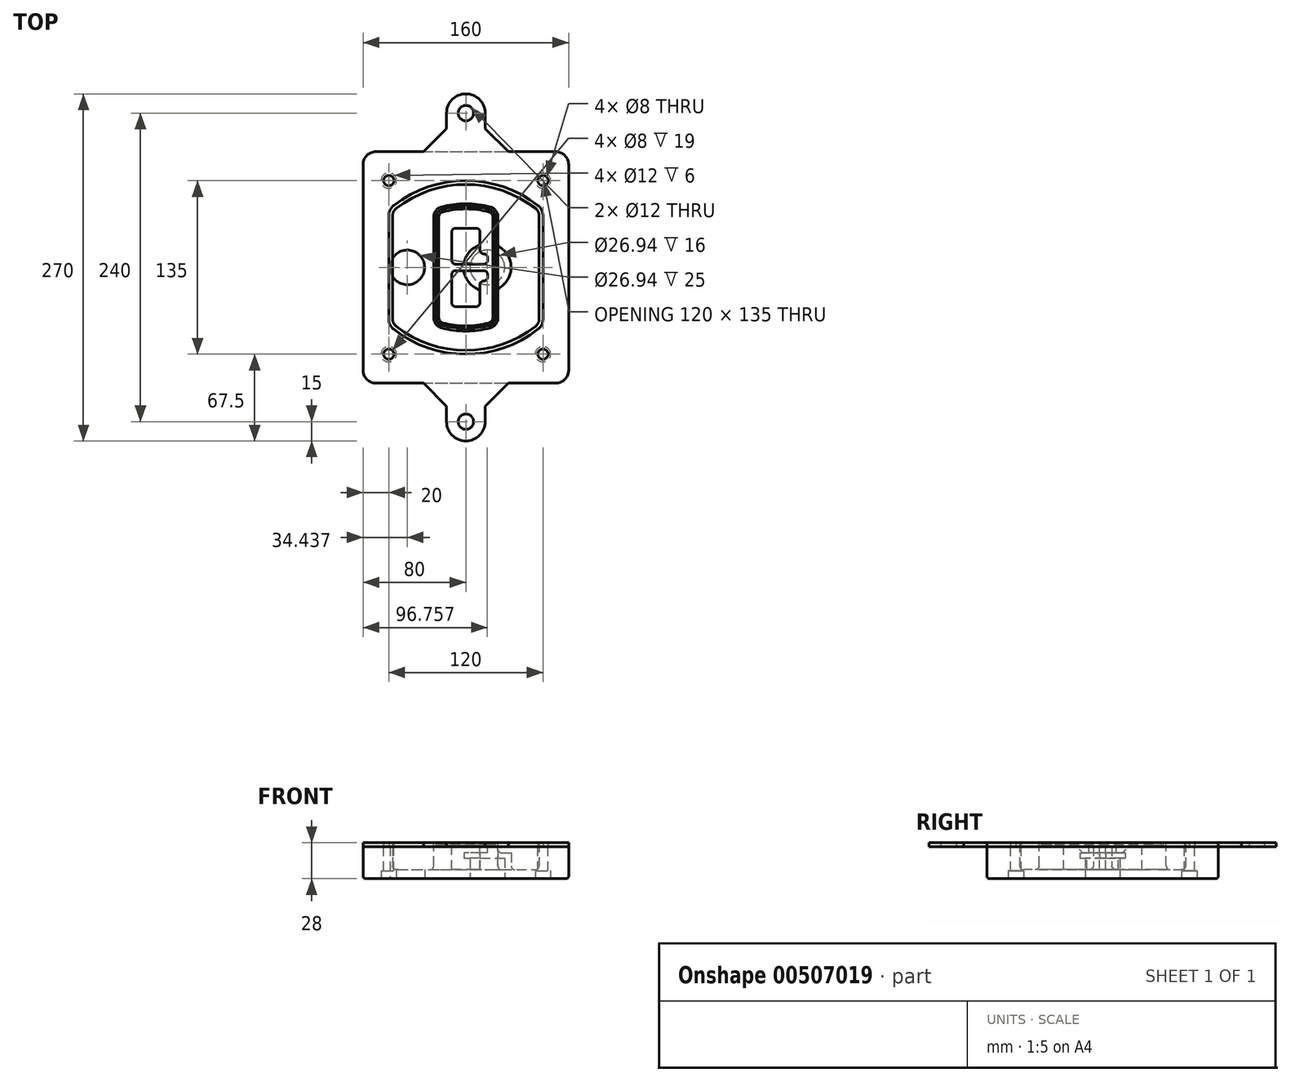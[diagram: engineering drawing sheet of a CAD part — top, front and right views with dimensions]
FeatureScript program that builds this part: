
annotation { "Feature Type Name" : "Feature", "Feature Type Description" : "" }
export const myFeature = defineFeature(function(context is Context, id is Id, definition is map)
    precondition{}
    {
        {
            var Q0;
            Q0=qCreatedBy(makeId("Top.planeOp"),FACE);
            var sketch = newSketch(context, id + "F0", { "sketchPlane" : qUnion([Q0])});
            skPoint(sketch, "E0.rect.middle", {"position": v(0, 0) * mm});
            skLineSegment(sketch, "E1.bottom", {"start": v(-70, -90) * mm, "end": v(70, -90) * mm});
            skLineSegment(sketch, "E1.top", {"start": v(-70, 90) * mm, "end": v(70, 90) * mm});
            skLineSegment(sketch, "E1.left", {"start": v(-80, -80) * mm, "end": v(-80, 80) * mm});
            skLineSegment(sketch, "E1.right", {"start": v(80, -80) * mm, "end": v(80, 80) * mm});
            skLineSegment(sketch, "E2", {"start": v(-80, 90) * mm, "end": v(80, -90) * mm, "construction": true});
            skLineSegment(sketch, "E3", {"start": v(80, 90) * mm, "end": v(-80, -90) * mm, "construction": true});
            skCircle(sketch, "E4", {"center": v(-60, 67.5) * mm, "radius": 4 * mm});
            skCircle(sketch, "E5", {"center": v(60, 67.5) * mm, "radius": 4 * mm});
            skCircle(sketch, "E6", {"center": v(60, -67.5) * mm, "radius": 4 * mm});
            skCircle(sketch, "E7", {"center": v(-60, -67.5) * mm, "radius": 4 * mm});
            skLineSegment(sketch, "E8", {"start": v(-60, 67.5) * mm, "end": v(60, 67.5) * mm, "construction": true});
            skLineSegment(sketch, "E9", {"start": v(60, 67.5) * mm, "end": v(60, -67.5) * mm, "construction": true});
            skLineSegment(sketch, "E10", {"start": v(60, -67.5) * mm, "end": v(-60, -67.5) * mm, "construction": true});
            skLineSegment(sketch, "E11", {"start": v(-60, -67.5) * mm, "end": v(-60, 67.5) * mm, "construction": true});
            skLineSegment(sketch, "E12", {"start": v(-60, 40.3) * mm, "end": v(-60, -40.3) * mm});
            skLineSegment(sketch, "E13", {"start": v(60, 40.3) * mm, "end": v(60, -40.3) * mm});
            skArc(sketch, "E14", {"start": v(56.15, 48.18) * mm, "mid": v(0, 67.5) * mm, "end": v(-56.15, 48.18) * mm});
            skArc(sketch, "E15", {"start": v(-56.15, -48.18) * mm, "mid": v(0, -67.5) * mm, "end": v(56.15, -48.18) * mm});
            skLineSegment(sketch, "E16", {"start": v(-60, 0) * mm, "end": v(60, 0) * mm, "construction": true});
            skPoint(sketch, "E17.visualSharp", {"position": v(-60, -45) * mm});
            skArc(sketch, "E17.filletArc", {"start": v(-60, -40.3) * mm, "mid": v(-58.99, -44.68) * mm, "end": v(-56.15, -48.18) * mm});
            skPoint(sketch, "E18.visualSharp", {"position": v(-60, 45) * mm});
            skArc(sketch, "E18.filletArc", {"start": v(-56.15, 48.18) * mm, "mid": v(-58.99, 44.68) * mm, "end": v(-60, 40.3) * mm});
            skPoint(sketch, "E19.visualSharp", {"position": v(60, 45) * mm});
            skArc(sketch, "E19.filletArc", {"start": v(60, 40.3) * mm, "mid": v(58.99, 44.68) * mm, "end": v(56.15, 48.18) * mm});
            skPoint(sketch, "E20.visualSharp", {"position": v(60, -45) * mm});
            skArc(sketch, "E20.filletArc", {"start": v(56.15, -48.18) * mm, "mid": v(58.99, -44.68) * mm, "end": v(60, -40.3) * mm});
            skPoint(sketch, "E21.visualSharp", {"position": v(-80, 90) * mm});
            skArc(sketch, "E21.filletArc", {"start": v(-70, 90) * mm, "mid": v(-77.07, 87.07) * mm, "end": v(-80, 80) * mm});
            skPoint(sketch, "E22.visualSharp", {"position": v(80, 90) * mm});
            skArc(sketch, "E22.filletArc", {"start": v(80, 80) * mm, "mid": v(77.07, 87.07) * mm, "end": v(70, 90) * mm});
            skPoint(sketch, "E23.visualSharp", {"position": v(80, -90) * mm});
            skArc(sketch, "E23.filletArc", {"start": v(70, -90) * mm, "mid": v(77.07, -87.07) * mm, "end": v(80, -80) * mm});
            skPoint(sketch, "E24.visualSharp", {"position": v(-80, -90) * mm});
            skArc(sketch, "E24.filletArc", {"start": v(-80, -80) * mm, "mid": v(-77.07, -87.07) * mm, "end": v(-70, -90) * mm});
            skArc(sketch, "E25.0", {"start": v(57, 40.3) * mm, "mid": v(56.3, 43.36) * mm, "end": v(54.3, 45.81) * mm});
            skLineSegment(sketch, "E25.1", {"start": v(57, 40.3) * mm, "end": v(57, -40.3) * mm});
            skArc(sketch, "E25.2", {"start": v(54.3, -45.81) * mm, "mid": v(56.3, -43.36) * mm, "end": v(57, -40.3) * mm});
            skArc(sketch, "E25.3", {"start": v(-54.3, -45.81) * mm, "mid": v(0, -64.5) * mm, "end": v(54.3, -45.81) * mm});
            skArc(sketch, "E25.4", {"start": v(-57, -40.3) * mm, "mid": v(-56.3, -43.36) * mm, "end": v(-54.3, -45.81) * mm});
            skArc(sketch, "E25.5", {"start": v(54.3, 45.81) * mm, "mid": v(0, 64.5) * mm, "end": v(-54.3, 45.81) * mm});
            skLineSegment(sketch, "E25.6", {"start": v(-57, 40.3) * mm, "end": v(-57, -40.3) * mm});
            skArc(sketch, "E25.7", {"start": v(-54.3, 45.81) * mm, "mid": v(-56.3, 43.36) * mm, "end": v(-57, 40.3) * mm});
            skArc(sketch, "E26.0", {"start": v(-58.62, 51.33) * mm, "mid": v(-62.58, 46.43) * mm, "end": v(-64, 40.3) * mm});
            skArc(sketch, "E26.1", {"start": v(58.62, 51.33) * mm, "mid": v(0, 71.5) * mm, "end": v(-58.62, 51.33) * mm});
            skArc(sketch, "E26.2", {"start": v(64, 40.3) * mm, "mid": v(62.58, 46.43) * mm, "end": v(58.62, 51.33) * mm});
            skLineSegment(sketch, "E26.3", {"start": v(64, 40.3) * mm, "end": v(64, -40.3) * mm});
            skArc(sketch, "E26.4", {"start": v(58.62, -51.33) * mm, "mid": v(62.58, -46.43) * mm, "end": v(64, -40.3) * mm});
            skLineSegment(sketch, "E26.5", {"start": v(-64, 40.3) * mm, "end": v(-64, -40.3) * mm});
            skArc(sketch, "E26.6", {"start": v(-58.62, -51.33) * mm, "mid": v(0, -71.5) * mm, "end": v(58.62, -51.33) * mm});
            skArc(sketch, "E26.7", {"start": v(-64, -40.3) * mm, "mid": v(-62.58, -46.43) * mm, "end": v(-58.62, -51.33) * mm});
            skSolve(sketch);
        }
        {
            var Q0;
            Q0=makeQuery(id+"F0.imprint","IMPRINT",FACE,{"disambiguationData":[TD([[makeQuery(id+"F0.imprint","IMPRINT",EDGE,{"derivedFrom":sQuery(id+"F0.wireOp",EDGE,"E1.bottom")}),1.0]])]});
            var Q1;
            Q1=makeQuery(id+"F0.imprint","IMPRINT",FACE,{"disambiguationData":[TD([[makeQuery(id+"F0.imprint","IMPRINT",EDGE,{"derivedFrom":sQuery(id+"F0.wireOp",EDGE,"E12")}),1.0]])]});
            var Q2;
            Q2=makeQuery(id+"F0.imprint","IMPRINT",FACE,{"disambiguationData":[TD([[makeQuery(id+"F0.imprint","IMPRINT",EDGE,{"derivedFrom":sQuery(id+"F0.wireOp",EDGE,"E25.0")}),1.0]])]});
            var Q3;
            Q3=makeQuery(id+"F0.imprint","IMPRINT",FACE,{"disambiguationData":[TD([[makeQuery(id+"F0.imprint","IMPRINT",EDGE,{"derivedFrom":sQuery(id+"F0.wireOp",EDGE,"E12")}),-1.0]])]});
            extrude(context, id + "F1", {"entities" : qUnion([Q0, Q1, Q2, Q3]), "oppositeDirection" : true, "depth" : 25 * mm});
        }
        {
            var Q0;
            Q0=makeQuery(id+"F0.imprint","IMPRINT",FACE,{"disambiguationData":[TD([[makeQuery(id+"F0.imprint","IMPRINT",EDGE,{"derivedFrom":sQuery(id+"F0.wireOp",EDGE,"E12")}),1.0]])]});
            extrude(context, id + "F2", {"entities" : qUnion([Q0]), "operationType" : NewBodyOperationType.ADD, "depth" : 3 * mm});
        }
        {
            var Q0;
            Q0=makeQuery(id+"F0.imprint","IMPRINT",FACE,{"disambiguationData":[TD([[makeQuery(id+"F0.imprint","IMPRINT",EDGE,{"derivedFrom":sQuery(id+"F0.wireOp",EDGE,"E25.0")}),1.0]])]});
            extrude(context, id + "F3", {"entities" : qUnion([Q0]), "operationType" : NewBodyOperationType.REMOVE, "oppositeDirection" : true, "depth" : 18 * mm});
        }
        {
            var Q0;
            Q0=makeQuery(id+"F2.opExtrude","CAP_FACE",FACE,{"disambiguationData":[OSD([sQuery(id+"F0.wireOp",EDGE,"E12"),sQuery(id+"F0.wireOp",EDGE,"E13"),sQuery(id+"F0.wireOp",EDGE,"E14"),sQuery(id+"F0.wireOp",EDGE,"E15"),sQuery(id+"F0.wireOp",EDGE,"E17.filletArc"),sQuery(id+"F0.wireOp",EDGE,"E18.filletArc"),sQuery(id+"F0.wireOp",EDGE,"E19.filletArc"),sQuery(id+"F0.wireOp",EDGE,"E20.filletArc"),sQuery(id+"F0.wireOp",EDGE,"E25.0"),sQuery(id+"F0.wireOp",EDGE,"E25.1"),sQuery(id+"F0.wireOp",EDGE,"E25.2"),sQuery(id+"F0.wireOp",EDGE,"E25.3"),sQuery(id+"F0.wireOp",EDGE,"E25.4"),sQuery(id+"F0.wireOp",EDGE,"E25.5"),sQuery(id+"F0.wireOp",EDGE,"E25.6"),sQuery(id+"F0.wireOp",EDGE,"E25.7")])],"isStart":false});
            var sketch = newSketch(context, id + "F4", { "sketchPlane" : qUnion([Q0])});
            skArc(sketch, "E27.0", {"start": v(-19.08, -46.97) * mm, "mid": v(0, -49.5) * mm, "end": v(19.08, -46.97) * mm});
            skArc(sketch, "E28.0", {"start": v(19.08, 46.97) * mm, "mid": v(0, 49.5) * mm, "end": v(-19.08, 46.97) * mm});
            skLineSegment(sketch, "E29", {"start": v(-25, 39.25) * mm, "end": v(-25, -39.25) * mm});
            skLineSegment(sketch, "E30", {"start": v(25, 39.25) * mm, "end": v(25, -39.25) * mm});
            skLineSegment(sketch, "E31", {"start": v(-25, 45.1) * mm, "end": v(25, 45.1) * mm, "construction": true});
            skLineSegment(sketch, "E32", {"start": v(-25, -45.1) * mm, "end": v(25, -45.1) * mm, "construction": true});
            skPoint(sketch, "E33.visualSharp", {"position": v(-25, 45.1) * mm});
            skArc(sketch, "E33.filletArc", {"start": v(-19.08, 46.97) * mm, "mid": v(-23.35, 44.11) * mm, "end": v(-25, 39.25) * mm});
            skPoint(sketch, "E34.visualSharp", {"position": v(25, 45.1) * mm});
            skArc(sketch, "E34.filletArc", {"start": v(25, 39.25) * mm, "mid": v(23.35, 44.11) * mm, "end": v(19.08, 46.97) * mm});
            skPoint(sketch, "E35.visualSharp", {"position": v(25, -45.1) * mm});
            skArc(sketch, "E35.filletArc", {"start": v(19.08, -46.97) * mm, "mid": v(23.35, -44.11) * mm, "end": v(25, -39.25) * mm});
            skPoint(sketch, "E36.visualSharp", {"position": v(-25, -45.1) * mm});
            skArc(sketch, "E36.filletArc", {"start": v(-25, -39.25) * mm, "mid": v(-23.35, -44.11) * mm, "end": v(-19.08, -46.97) * mm});
            skArc(sketch, "E37.0", {"start": v(54.3, 45.81) * mm, "mid": v(0, 64.5) * mm, "end": v(-54.3, 45.81) * mm});
            skArc(sketch, "E37.1", {"start": v(-54.3, 45.81) * mm, "mid": v(-56.3, 43.36) * mm, "end": v(-57, 40.3) * mm});
            skLineSegment(sketch, "E37.2", {"start": v(-57, 40.3) * mm, "end": v(-57, -40.3) * mm});
            skArc(sketch, "E37.3", {"start": v(-57, -40.3) * mm, "mid": v(-56.3, -43.36) * mm, "end": v(-54.3, -45.81) * mm});
            skArc(sketch, "E37.4", {"start": v(-54.3, -45.81) * mm, "mid": v(0, -64.5) * mm, "end": v(54.3, -45.81) * mm});
            skArc(sketch, "E37.5", {"start": v(54.3, -45.81) * mm, "mid": v(56.3, -43.36) * mm, "end": v(57, -40.3) * mm});
            skLineSegment(sketch, "E37.6", {"start": v(57, 40.3) * mm, "end": v(57, -40.3) * mm});
            skArc(sketch, "E37.7", {"start": v(57, 40.3) * mm, "mid": v(56.3, 43.36) * mm, "end": v(54.3, 45.81) * mm});
            skLineSegment(sketch, "E38.0", {"start": v(23, 39.25) * mm, "end": v(23, -39.25) * mm});
            skArc(sketch, "E38.1", {"start": v(18.56, -45.04) * mm, "mid": v(21.76, -42.9) * mm, "end": v(23, -39.25) * mm});
            skArc(sketch, "E38.2", {"start": v(-18.56, -45.04) * mm, "mid": v(0, -47.5) * mm, "end": v(18.56, -45.04) * mm});
            skArc(sketch, "E38.3", {"start": v(-23, -39.25) * mm, "mid": v(-21.76, -42.9) * mm, "end": v(-18.56, -45.04) * mm});
            skLineSegment(sketch, "E38.4", {"start": v(-23, 39.25) * mm, "end": v(-23, -39.25) * mm});
            skArc(sketch, "E38.5", {"start": v(23, 39.25) * mm, "mid": v(21.76, 42.9) * mm, "end": v(18.56, 45.04) * mm});
            skArc(sketch, "E38.6", {"start": v(-18.56, 45.04) * mm, "mid": v(-21.76, 42.9) * mm, "end": v(-23, 39.25) * mm});
            skArc(sketch, "E38.7", {"start": v(18.56, 45.04) * mm, "mid": v(0, 47.5) * mm, "end": v(-18.56, 45.04) * mm});
            skArc(sketch, "E39.0", {"start": v(21, 39.25) * mm, "mid": v(20.18, 41.68) * mm, "end": v(18.04, 43.1) * mm});
            skLineSegment(sketch, "E39.1", {"start": v(21, 39.25) * mm, "end": v(21, -39.25) * mm});
            skArc(sketch, "E39.2", {"start": v(18.04, -43.1) * mm, "mid": v(20.18, -41.68) * mm, "end": v(21, -39.25) * mm});
            skArc(sketch, "E39.3", {"start": v(-18.04, -43.1) * mm, "mid": v(0, -45.5) * mm, "end": v(18.04, -43.1) * mm});
            skArc(sketch, "E39.4", {"start": v(-21, -39.25) * mm, "mid": v(-20.18, -41.68) * mm, "end": v(-18.04, -43.1) * mm});
            skArc(sketch, "E39.5", {"start": v(18.04, 43.1) * mm, "mid": v(0, 45.5) * mm, "end": v(-18.04, 43.1) * mm});
            skLineSegment(sketch, "E39.6", {"start": v(-21, 39.25) * mm, "end": v(-21, -39.25) * mm});
            skArc(sketch, "E39.7", {"start": v(-18.04, 43.1) * mm, "mid": v(-20.18, 41.68) * mm, "end": v(-21, 39.25) * mm});
            skLineSegment(sketch, "E40", {"start": v(-25, 0) * mm, "end": v(25, 0) * mm, "construction": true});
            skLineSegment(sketch, "E41", {"start": v(-11, 5.5) * mm, "end": v(-11, 27.5) * mm});
            skLineSegment(sketch, "E42", {"start": v(-8, 30.5) * mm, "end": v(8, 30.5) * mm});
            skLineSegment(sketch, "E43", {"start": v(11, 27.5) * mm, "end": v(11, 13.5) * mm});
            skLineSegment(sketch, "E44", {"start": v(14, 10.5) * mm, "end": v(14, 10.5) * mm});
            skLineSegment(sketch, "E45", {"start": v(17, 7.5) * mm, "end": v(17, 5.5) * mm});
            skLineSegment(sketch, "E46", {"start": v(14, 2.5) * mm, "end": v(-8, 2.5) * mm});
            skPoint(sketch, "E47.visualSharp", {"position": v(-11, 30.5) * mm});
            skArc(sketch, "E47.filletArc", {"start": v(-8, 30.5) * mm, "mid": v(-10.12, 29.62) * mm, "end": v(-11, 27.5) * mm});
            skPoint(sketch, "E48.visualSharp", {"position": v(11, 30.5) * mm});
            skArc(sketch, "E48.filletArc", {"start": v(11, 27.5) * mm, "mid": v(10.12, 29.62) * mm, "end": v(8, 30.5) * mm});
            skPoint(sketch, "E49.visualSharp", {"position": v(11, 10.5) * mm});
            skArc(sketch, "E49.filletArc", {"start": v(11, 13.5) * mm, "mid": v(11.88, 11.38) * mm, "end": v(14, 10.5) * mm});
            skPoint(sketch, "E50.visualSharp", {"position": v(17, 10.5) * mm});
            skArc(sketch, "E50.filletArc", {"start": v(17, 7.5) * mm, "mid": v(16.12, 9.62) * mm, "end": v(14, 10.5) * mm});
            skPoint(sketch, "E51.visualSharp", {"position": v(17, 2.5) * mm});
            skArc(sketch, "E51.filletArc", {"start": v(14, 2.5) * mm, "mid": v(16.12, 3.38) * mm, "end": v(17, 5.5) * mm});
            skPoint(sketch, "E52.visualSharp", {"position": v(-11, 2.5) * mm});
            skArc(sketch, "E52.filletArc", {"start": v(-11, 5.5) * mm, "mid": v(-10.12, 3.38) * mm, "end": v(-8, 2.5) * mm});
            skLineSegment(sketch, "E53.0.MirrorCS", {"start": v(14, -2.5) * mm, "end": v(-8, -2.5) * mm});
            skArc(sketch, "E54.0.MirrorCS", {"start": v(-11, -5.5) * mm, "mid": v(-10.12, -3.38) * mm, "end": v(-8, -2.5) * mm});
            skLineSegment(sketch, "E55.0.MirrorCS", {"start": v(-11, -5.5) * mm, "end": v(-11, -27.5) * mm});
            skArc(sketch, "E56.0.MirrorCS", {"start": v(-8, -30.5) * mm, "mid": v(-10.12, -29.62) * mm, "end": v(-11, -27.5) * mm});
            skLineSegment(sketch, "E57.0.MirrorCS", {"start": v(-8, -30.5) * mm, "end": v(8, -30.5) * mm});
            skArc(sketch, "E58.0.MirrorCS", {"start": v(11, -27.5) * mm, "mid": v(10.12, -29.62) * mm, "end": v(8, -30.5) * mm});
            skLineSegment(sketch, "E59.0.MirrorCS", {"start": v(11, -27.5) * mm, "end": v(11, -13.5) * mm});
            skArc(sketch, "E60.0.MirrorCS", {"start": v(11, -13.5) * mm, "mid": v(11.88, -11.38) * mm, "end": v(14, -10.5) * mm});
            skArc(sketch, "E61.0.MirrorCS", {"start": v(17, -7.5) * mm, "mid": v(16.12, -9.62) * mm, "end": v(14, -10.5) * mm});
            skLineSegment(sketch, "E62.0.MirrorCS", {"start": v(17, -7.5) * mm, "end": v(17, -5.5) * mm});
            skArc(sketch, "E63.0.MirrorCS", {"start": v(14, -2.5) * mm, "mid": v(16.12, -3.38) * mm, "end": v(17, -5.5) * mm});
            skSolve(sketch);
        }
        {
            var Q0;
            Q0=makeQuery(id+"F4.imprint","IMPRINT",FACE,{"disambiguationData":[TD([[makeQuery(id+"F4.imprint","IMPRINT",EDGE,{"derivedFrom":sQuery(id+"F4.wireOp",EDGE,"E27.0")}),1.0]])]});
            var Q1;
            Q1=makeQuery(id+"F4.imprint","IMPRINT",FACE,{"disambiguationData":[TD([[makeQuery(id+"F4.imprint","IMPRINT",EDGE,{"derivedFrom":sQuery(id+"F4.wireOp",EDGE,"E38.0")}),-1.0]])]});
            var Q2;
            Q2=makeQuery(id+"F4.imprint","IMPRINT",FACE,{"disambiguationData":[TD([[makeQuery(id+"F4.imprint","IMPRINT",EDGE,{"derivedFrom":sQuery(id+"F4.wireOp",EDGE,"E39.0")}),1.0]])]});
            extrude(context, id + "F5", {"entities" : qUnion([Q0, Q1, Q2]), "operationType" : NewBodyOperationType.ADD, "endBound" : BoundingType.UP_TO_NEXT, "oppositeDirection" : true, "depth" : 25 * mm});
        }
        {
            var Q0;
            Q0=makeQuery(id+"F4.imprint","IMPRINT",FACE,{"disambiguationData":[TD([[makeQuery(id+"F4.imprint","IMPRINT",EDGE,{"derivedFrom":sQuery(id+"F4.wireOp",EDGE,"E38.0")}),-1.0]])]});
            extrude(context, id + "F6", {"entities" : qUnion([Q0]), "operationType" : NewBodyOperationType.REMOVE, "oppositeDirection" : true, "depth" : 2 * mm});
        }
        {
            var Q0;
            Q0=makeQuery(id+"F1.opExtrude","CAP_FACE",FACE,{"disambiguationData":[OSD([sQuery(id+"F0.wireOp",EDGE,"E1.bottom"),sQuery(id+"F0.wireOp",EDGE,"E1.top"),sQuery(id+"F0.wireOp",EDGE,"E1.left"),sQuery(id+"F0.wireOp",EDGE,"E1.right"),sQuery(id+"F0.wireOp",EDGE,"E4"),sQuery(id+"F0.wireOp",EDGE,"E5"),sQuery(id+"F0.wireOp",EDGE,"E6"),sQuery(id+"F0.wireOp",EDGE,"E7"),sQuery(id+"F0.wireOp",EDGE,"E21.filletArc"),sQuery(id+"F0.wireOp",EDGE,"E22.filletArc"),sQuery(id+"F0.wireOp",EDGE,"E23.filletArc"),sQuery(id+"F0.wireOp",EDGE,"E24.filletArc")])],"isStart":false});
            var sketch = newSketch(context, id + "F7", { "sketchPlane" : qUnion([Q0])});
            skCircle(sketch, "E64", {"center": v(16.76, 0) * mm, "radius": 13.47 * mm});
            skCircle(sketch, "E65", {"center": v(-45.56, 0) * mm, "radius": 13.47 * mm});
            skLineSegment(sketch, "E66", {"start": v(80, 0) * mm, "end": v(-80, 0) * mm});
            skCircle(sketch, "E67", {"center": v(16.76, 0) * mm, "radius": 18.47 * mm});
            skCircle(sketch, "E68", {"center": v(60, -67.5) * mm, "radius": 6 * mm});
            skCircle(sketch, "E69", {"center": v(-60, -67.5) * mm, "radius": 6 * mm});
            skCircle(sketch, "E70", {"center": v(-60, 67.5) * mm, "radius": 6 * mm});
            skCircle(sketch, "E71", {"center": v(60, 67.5) * mm, "radius": 6 * mm});
            skSolve(sketch);
        }
        {
            var Q0;
            {var subQ1=sQuery(id+"F7.wireOp",EDGE,"E66");var subQ4=sQuery(id+"F7.wireOp",EDGE,"E64");var subQ6=makeQuery(id+"F7.imprint","INTERSECT",VERTEX,{"disambiguationData":[OD(0.0)],"derivedFrom":[subQ4,subQ1]});Q0=makeQuery(id+"F7.imprint","IMPRINT",FACE,{"disambiguationData":[TD([[makeQuery(id+"F7.imprint","IMPRINT",EDGE,{"disambiguationData":[TD([[subQ6,-1.0]])],"derivedFrom":subQ4}),-1.0]])]});}
            var Q1;
            {var subQ0=sQuery(id+"F7.wireOp",EDGE,"E66");var subQ1=sQuery(id+"F7.wireOp",EDGE,"E64");var subQ3=makeQuery(id+"F7.imprint","INTERSECT",VERTEX,{"disambiguationData":[OD(0.0)],"derivedFrom":[subQ1,subQ0]});Q1=makeQuery(id+"F7.imprint","IMPRINT",FACE,{"disambiguationData":[TD([[makeQuery(id+"F7.imprint","IMPRINT",EDGE,{"disambiguationData":[TD([[subQ3,-1.0]])],"derivedFrom":subQ1}),1.0]])]});}
            var Q2;
            {var subQ0=sQuery(id+"F7.wireOp",EDGE,"E66");var subQ1=sQuery(id+"F7.wireOp",EDGE,"E64");var subQ3=makeQuery(id+"F7.imprint","INTERSECT",VERTEX,{"disambiguationData":[OD(0.0)],"derivedFrom":[subQ1,subQ0]});Q2=makeQuery(id+"F7.imprint","IMPRINT",FACE,{"disambiguationData":[TD([[makeQuery(id+"F7.imprint","IMPRINT",EDGE,{"disambiguationData":[TD([[subQ3,1.0]])],"derivedFrom":subQ1}),1.0]])]});}
            var Q3;
            {var subQ1=sQuery(id+"F7.wireOp",EDGE,"E66");var subQ4=sQuery(id+"F7.wireOp",EDGE,"E64");var subQ6=makeQuery(id+"F7.imprint","INTERSECT",VERTEX,{"disambiguationData":[OD(0.0)],"derivedFrom":[subQ4,subQ1]});Q3=makeQuery(id+"F7.imprint","IMPRINT",FACE,{"disambiguationData":[TD([[makeQuery(id+"F7.imprint","IMPRINT",EDGE,{"disambiguationData":[TD([[subQ6,1.0]])],"derivedFrom":subQ4}),-1.0]])]});}
            extrude(context, id + "F8", {"entities" : qUnion([Q0, Q1, Q2, Q3]), "operationType" : NewBodyOperationType.ADD, "oppositeDirection" : true, "depth" : 20 * mm});
        }
        {
            var Q0;
            {var subQ0=sQuery(id+"F7.wireOp",EDGE,"E66");var subQ1=sQuery(id+"F7.wireOp",EDGE,"E64");var subQ3=makeQuery(id+"F7.imprint","INTERSECT",VERTEX,{"disambiguationData":[OD(0.0)],"derivedFrom":[subQ1,subQ0]});Q0=makeQuery(id+"F7.imprint","IMPRINT",FACE,{"disambiguationData":[TD([[makeQuery(id+"F7.imprint","IMPRINT",EDGE,{"disambiguationData":[TD([[subQ3,-1.0]])],"derivedFrom":subQ1}),1.0]])]});}
            var Q1;
            {var subQ0=sQuery(id+"F7.wireOp",EDGE,"E66");var subQ1=sQuery(id+"F7.wireOp",EDGE,"E64");var subQ3=makeQuery(id+"F7.imprint","INTERSECT",VERTEX,{"disambiguationData":[OD(0.0)],"derivedFrom":[subQ1,subQ0]});Q1=makeQuery(id+"F7.imprint","IMPRINT",FACE,{"disambiguationData":[TD([[makeQuery(id+"F7.imprint","IMPRINT",EDGE,{"disambiguationData":[TD([[subQ3,1.0]])],"derivedFrom":subQ1}),1.0]])]});}
            extrude(context, id + "F9", {"entities" : qUnion([Q0, Q1]), "operationType" : NewBodyOperationType.REMOVE, "oppositeDirection" : true, "depth" : 16 * mm});
        }
        {
            var Q0;
            {var subQ0=sQuery(id+"F7.wireOp",EDGE,"E66");var subQ1=sQuery(id+"F7.wireOp",EDGE,"E65");var subQ3=makeQuery(id+"F7.imprint","INTERSECT",VERTEX,{"disambiguationData":[OD(0.0)],"derivedFrom":[subQ1,subQ0]});Q0=makeQuery(id+"F7.imprint","IMPRINT",FACE,{"disambiguationData":[TD([[makeQuery(id+"F7.imprint","IMPRINT",EDGE,{"disambiguationData":[TD([[subQ3,-1.0]])],"derivedFrom":subQ1}),1.0]])]});}
            var Q1;
            {var subQ0=sQuery(id+"F7.wireOp",EDGE,"E66");var subQ1=sQuery(id+"F7.wireOp",EDGE,"E65");var subQ3=makeQuery(id+"F7.imprint","INTERSECT",VERTEX,{"disambiguationData":[OD(0.0)],"derivedFrom":[subQ1,subQ0]});Q1=makeQuery(id+"F7.imprint","IMPRINT",FACE,{"disambiguationData":[TD([[makeQuery(id+"F7.imprint","IMPRINT",EDGE,{"disambiguationData":[TD([[subQ3,1.0]])],"derivedFrom":subQ1}),1.0]])]});}
            extrude(context, id + "F10", {"entities" : qUnion([Q0, Q1]), "operationType" : NewBodyOperationType.REMOVE, "oppositeDirection" : true, "depth" : 25 * mm});
        }
        {
            var Q0;
            Q0=makeQuery(id+"F7.imprint","IMPRINT",FACE,{"disambiguationData":[TD([[makeQuery(id+"F7.imprint","IMPRINT",EDGE,{"derivedFrom":sQuery(id+"F7.wireOp",EDGE,"E68")}),1.0]])]});
            var Q1;
            Q1=makeQuery(id+"F7.imprint","IMPRINT",FACE,{"disambiguationData":[TD([[makeQuery(id+"F7.imprint","IMPRINT",EDGE,{"derivedFrom":makeQuery(id+"F1.opExtrude","CAP_EDGE",EDGE,{"disambiguationData":[OSD([sQuery(id+"F0.wireOp",EDGE,"E5")])],"isStart":false})}),-1.0]])]});
            var Q2;
            Q2=makeQuery(id+"F7.imprint","IMPRINT",FACE,{"disambiguationData":[TD([[makeQuery(id+"F7.imprint","IMPRINT",EDGE,{"derivedFrom":sQuery(id+"F7.wireOp",EDGE,"E69")}),1.0]])]});
            var Q3;
            Q3=makeQuery(id+"F7.imprint","IMPRINT",FACE,{"disambiguationData":[TD([[makeQuery(id+"F7.imprint","IMPRINT",EDGE,{"derivedFrom":makeQuery(id+"F1.opExtrude","CAP_EDGE",EDGE,{"disambiguationData":[OSD([sQuery(id+"F0.wireOp",EDGE,"E4")])],"isStart":false})}),-1.0]])]});
            var Q4;
            Q4=makeQuery(id+"F7.imprint","IMPRINT",FACE,{"disambiguationData":[TD([[makeQuery(id+"F7.imprint","IMPRINT",EDGE,{"derivedFrom":sQuery(id+"F7.wireOp",EDGE,"E70")}),1.0]])]});
            var Q5;
            Q5=makeQuery(id+"F7.imprint","IMPRINT",FACE,{"disambiguationData":[TD([[makeQuery(id+"F7.imprint","IMPRINT",EDGE,{"derivedFrom":makeQuery(id+"F1.opExtrude","CAP_EDGE",EDGE,{"disambiguationData":[OSD([sQuery(id+"F0.wireOp",EDGE,"E7")])],"isStart":false})}),-1.0]])]});
            var Q6;
            Q6=makeQuery(id+"F7.imprint","IMPRINT",FACE,{"disambiguationData":[TD([[makeQuery(id+"F7.imprint","IMPRINT",EDGE,{"derivedFrom":sQuery(id+"F7.wireOp",EDGE,"E71")}),1.0]])]});
            var Q7;
            Q7=makeQuery(id+"F7.imprint","IMPRINT",FACE,{"disambiguationData":[TD([[makeQuery(id+"F7.imprint","IMPRINT",EDGE,{"derivedFrom":makeQuery(id+"F1.opExtrude","CAP_EDGE",EDGE,{"disambiguationData":[OSD([sQuery(id+"F0.wireOp",EDGE,"E6")])],"isStart":false})}),-1.0]])]});
            extrude(context, id + "F11", {"entities" : qUnion([Q0, Q1, Q2, Q3, Q4, Q5, Q6, Q7]), "operationType" : NewBodyOperationType.REMOVE, "oppositeDirection" : true, "depth" : 6 * mm});
        }
        {
            var Q0;
            Q0=makeQuery(id+"F9.boolean.opBoolean","COPY",FACE,{"derivedFrom":makeQuery(id+"F9.opExtrude","CAP_FACE",FACE,{"disambiguationData":[OSD([sQuery(id+"F7.wireOp",EDGE,"E64")])],"isStart":false})});
            var sketch = newSketch(context, id + "F12", { "sketchPlane" : qUnion([Q0])});
            skArc(sketch, "E72.0", {"start": v(11, 17.55) * mm, "mid": v(2.57, 11.82) * mm, "end": v(-1.54, 2.5) * mm});
            skArc(sketch, "E72.1", {"start": v(-1.54, -2.5) * mm, "mid": v(2.57, -11.82) * mm, "end": v(11, -17.55) * mm});
            skLineSegment(sketch, "E73", {"start": v(-1.54, -2.5) * mm, "end": v(14, -2.5) * mm});
            skLineSegment(sketch, "E74.0", {"start": v(14, 2.5) * mm, "end": v(-1.54, 2.5) * mm});
            skArc(sketch, "E74.1", {"start": v(14, 2.5) * mm, "mid": v(16.12, 3.38) * mm, "end": v(17, 5.5) * mm});
            skLineSegment(sketch, "E74.2", {"start": v(17, 7.5) * mm, "end": v(17, 5.5) * mm});
            skArc(sketch, "E74.3", {"start": v(17, 7.5) * mm, "mid": v(16.12, 9.62) * mm, "end": v(14, 10.5) * mm});
            skArc(sketch, "E74.4", {"start": v(11, 13.5) * mm, "mid": v(11.88, 11.38) * mm, "end": v(14, 10.5) * mm});
            skLineSegment(sketch, "E74.5", {"start": v(11, 17.55) * mm, "end": v(11, 13.5) * mm});
            skLineSegment(sketch, "E74.7", {"start": v(14, -2.5) * mm, "end": v(-1.54, -2.5) * mm});
            skArc(sketch, "E74.8", {"start": v(14, -2.5) * mm, "mid": v(16.12, -3.38) * mm, "end": v(17, -5.5) * mm});
            skLineSegment(sketch, "E74.9", {"start": v(17, -7.5) * mm, "end": v(17, -5.5) * mm});
            skArc(sketch, "E74.10", {"start": v(17, -7.5) * mm, "mid": v(16.12, -9.62) * mm, "end": v(14, -10.5) * mm});
            skArc(sketch, "E74.11", {"start": v(11, -13.5) * mm, "mid": v(11.88, -11.38) * mm, "end": v(14, -10.5) * mm});
            skLineSegment(sketch, "E74.12", {"start": v(11, -17.55) * mm, "end": v(11, -13.5) * mm});
            skPoint(sketch, "E75.orphan", {"position": v(11, -27.5) * mm});
            skPoint(sketch, "E76.orphan", {"position": v(-8, -2.5) * mm});
            skPoint(sketch, "E77.orphan", {"position": v(-8, 2.5) * mm});
            skPoint(sketch, "E78.orphan", {"position": v(11, 27.5) * mm});
            skSolve(sketch);
        }
        {
            var Q0;
            {var subQ7=sQuery(id+"F12.wireOp",EDGE,"E72.0");var subQ14=sQuery(id+"F12.wireOp",EDGE,"E72.1");var subQ16=sQuery(id+"F12.wireOp",EDGE,"E74.1");var subQ18=sQuery(id+"F12.wireOp",EDGE,"E74.8");Q0=qUnion([makeQuery(id+"F12.imprint","IMPRINT",FACE,{"disambiguationData":[TD([[makeQuery(id+"F12.imprint","IMPRINT",EDGE,{"derivedFrom":subQ7}),1.0]])]}),makeQuery(id+"F12.imprint","IMPRINT",FACE,{"disambiguationData":[TD([[makeQuery(id+"F12.imprint","IMPRINT",EDGE,{"derivedFrom":subQ14}),1.0]])]}),makeQuery(id+"F12.imprint","IMPRINT",FACE,{"disambiguationData":[TD([[makeQuery(id+"F12.imprint","IMPRINT",EDGE,{"derivedFrom":subQ16}),1.0]])]}),makeQuery(id+"F12.imprint","IMPRINT",FACE,{"disambiguationData":[TD([[makeQuery(id+"F12.imprint","IMPRINT",EDGE,{"derivedFrom":subQ18}),-1.0]])]})]);}
            var Q1;
            Q1=makeQuery(id+"F5.boolean.opBoolean","SPLIT",FACE,{"disambiguationData":[TD([makeQuery(id+"F5.opExtrude","SWEPT_FACE",FACE,{"disambiguationData":[OSD([sQuery(id+"F4.wireOp",EDGE,"E41")])]})])],"derivedFrom":makeQuery(id+"F3.boolean.opBoolean","COPY",FACE,{"derivedFrom":makeQuery(id+"F3.opExtrude","CAP_FACE",FACE,{"disambiguationData":[OSD([sQuery(id+"F0.wireOp",EDGE,"E25.0"),sQuery(id+"F0.wireOp",EDGE,"E25.1"),sQuery(id+"F0.wireOp",EDGE,"E25.2"),sQuery(id+"F0.wireOp",EDGE,"E25.3"),sQuery(id+"F0.wireOp",EDGE,"E25.4"),sQuery(id+"F0.wireOp",EDGE,"E25.5"),sQuery(id+"F0.wireOp",EDGE,"E25.6"),sQuery(id+"F0.wireOp",EDGE,"E25.7")])],"isStart":false})})});
            extrude(context, id + "F13", {"entities" : qUnion([Q0]), "operationType" : NewBodyOperationType.REMOVE, "endBound" : BoundingType.UP_TO_SURFACE, "endBoundEntityFace" : qUnion([Q1]), "depth" : 25 * mm});
        }
        {
            var Q0;
            Q0=makeQuery(id+"F3.boolean.opBoolean","COPY",EDGE,{"derivedFrom":makeQuery(id+"F3.opExtrude","CAP_EDGE",EDGE,{"disambiguationData":[OSD([sQuery(id+"F0.wireOp",EDGE,"E25.6")])],"isStart":false})});
            var Q1;
            Q1=makeQuery(id+"F8.boolean.opBoolean","INTERSECT",EDGE,{"derivedFrom":[makeQuery(id+"F5.opExtrude","SWEPT_FACE",FACE,{"disambiguationData":[OSD([sQuery(id+"F4.wireOp",EDGE,"E30")])]}),makeQuery(id+"F8.opExtrude","CAP_FACE",FACE,{"disambiguationData":[OSD([sQuery(id+"F7.wireOp",EDGE,"E67")])],"isStart":false})]});
            var Q2;
            Q2=makeQuery(id+"F8.boolean.opBoolean","INTERSECT",EDGE,{"disambiguationData":[OD(1.0)],"derivedFrom":[makeQuery(id+"F5.opExtrude","SWEPT_FACE",FACE,{"disambiguationData":[OSD([sQuery(id+"F4.wireOp",EDGE,"E30")])]}),makeQuery(id+"F8.opExtrude","SWEPT_FACE",FACE,{"disambiguationData":[OSD([sQuery(id+"F7.wireOp",EDGE,"E67")])]})]});
            var Q3;
            {var subQ0=sQuery(id+"F4.wireOp",EDGE,"E30");Q3=makeQuery(id+"F8.boolean.opBoolean","SPLIT",EDGE,{"disambiguationData":[TD([makeQuery(id+"F5.opExtrude","SWEPT_FACE",FACE,{"disambiguationData":[OSD([sQuery(id+"F4.wireOp",EDGE,"E35.filletArc")])]})])],"derivedFrom":makeQuery(id+"F5.opExtrude","CAP_EDGE",EDGE,{"disambiguationData":[OSD([subQ0])],"isStart":false})});}
            var Q4;
            {var subQ0=sQuery(id+"F0.wireOp",EDGE,"E25.7");var subQ1=sQuery(id+"F0.wireOp",EDGE,"E25.1");var subQ2=sQuery(id+"F0.wireOp",EDGE,"E25.6");var subQ3=sQuery(id+"F0.wireOp",EDGE,"E25.5");var subQ4=sQuery(id+"F0.wireOp",EDGE,"E25.4");var subQ5=sQuery(id+"F0.wireOp",EDGE,"E25.0");var subQ6=sQuery(id+"F0.wireOp",EDGE,"E25.2");var subQ7=sQuery(id+"F0.wireOp",EDGE,"E25.3");Q4=makeQuery(id+"F8.boolean.opBoolean","INTERSECT",EDGE,{"derivedFrom":[makeQuery(id+"F5.boolean.opBoolean","SPLIT",FACE,{"disambiguationData":[TD([makeQuery(id+"F2.opExtrude","SWEPT_FACE",FACE,{"disambiguationData":[OSD([subQ5])]})])],"derivedFrom":makeQuery(id+"F3.boolean.opBoolean","COPY",FACE,{"derivedFrom":makeQuery(id+"F3.opExtrude","CAP_FACE",FACE,{"disambiguationData":[OSD([subQ5,subQ1,subQ6,subQ7,subQ4,subQ3,subQ2,subQ0])],"isStart":false})})}),makeQuery(id+"F8.opExtrude","SWEPT_FACE",FACE,{"disambiguationData":[OSD([sQuery(id+"F7.wireOp",EDGE,"E67")])]})]});}
            var Q5;
            Q5=makeQuery(id+"F8.boolean.opBoolean","INTERSECT",EDGE,{"disambiguationData":[OD(0.0)],"derivedFrom":[makeQuery(id+"F5.opExtrude","SWEPT_FACE",FACE,{"disambiguationData":[OSD([sQuery(id+"F4.wireOp",EDGE,"E30")])]}),makeQuery(id+"F8.opExtrude","SWEPT_FACE",FACE,{"disambiguationData":[OSD([sQuery(id+"F7.wireOp",EDGE,"E67")])]})]});
            fillet(context, id + "F14", {"entities" : qUnion([Q0, Q1, Q2, Q3, Q4, Q5]), "radius" : 3 * mm, "tangentPropagation" : true, "allowEdgeOverflow" : false});
        }
        {
            var Q0;
            Q0=makeQuery(id+"F1.opExtrude","CAP_EDGE",EDGE,{"disambiguationData":[OSD([sQuery(id+"F0.wireOp",EDGE,"E1.bottom")])],"isStart":false});
            fillet(context, id + "F15", {"entities" : qUnion([Q0]), "radius" : 2 * mm, "tangentPropagation" : true, "allowEdgeOverflow" : false});
        }
        {
            var Q0;
            {var subQ0=sQuery(id+"F0.wireOp",EDGE,"E21.filletArc");var subQ1=sQuery(id+"F0.wireOp",EDGE,"E7");var subQ2=sQuery(id+"F0.wireOp",EDGE,"E6");var subQ3=sQuery(id+"F0.wireOp",EDGE,"E5");var subQ4=sQuery(id+"F0.wireOp",EDGE,"E4");var subQ5=sQuery(id+"F0.wireOp",EDGE,"E22.filletArc");var subQ6=sQuery(id+"F0.wireOp",EDGE,"E1.bottom");var subQ7=sQuery(id+"F0.wireOp",EDGE,"E1.right");var subQ8=sQuery(id+"F0.wireOp",EDGE,"E1.top");var subQ9=sQuery(id+"F0.wireOp",EDGE,"E1.left");var subQ10=sQuery(id+"F0.wireOp",EDGE,"E23.filletArc");var subQ11=sQuery(id+"F0.wireOp",EDGE,"E24.filletArc");Q0=makeQuery(id+"F2.boolean.opBoolean","SPLIT",FACE,{"disambiguationData":[TD([makeQuery(id+"F1.opExtrude","SWEPT_FACE",FACE,{"disambiguationData":[OSD([subQ6])]})])],"derivedFrom":makeQuery(id+"F1.opExtrude","CAP_FACE",FACE,{"disambiguationData":[OSD([subQ6,subQ8,subQ9,subQ7,subQ4,subQ3,subQ2,subQ1,subQ0,subQ5,subQ10,subQ11])],"isStart":true})});}
            var sketch = newSketch(context, id + "F16", { "sketchPlane" : qUnion([Q0])});
            skLineSegment(sketch, "E79.0", {"start": v(60, 40.3) * mm, "end": v(60, -40.3) * mm});
            skArc(sketch, "E79.1", {"start": v(60, 40.3) * mm, "mid": v(58.99, 44.68) * mm, "end": v(56.15, 48.18) * mm});
            skArc(sketch, "E79.2", {"start": v(56.15, 48.18) * mm, "mid": v(0, 67.5) * mm, "end": v(-56.15, 48.18) * mm});
            skArc(sketch, "E79.3", {"start": v(-56.15, 48.18) * mm, "mid": v(-58.99, 44.68) * mm, "end": v(-60, 40.3) * mm});
            skLineSegment(sketch, "E79.4", {"start": v(-60, 40.3) * mm, "end": v(-60, -40.3) * mm});
            skArc(sketch, "E79.5", {"start": v(-60, -40.3) * mm, "mid": v(-58.99, -44.68) * mm, "end": v(-56.15, -48.18) * mm});
            skArc(sketch, "E79.6", {"start": v(-56.15, -48.18) * mm, "mid": v(0, -67.5) * mm, "end": v(56.15, -48.18) * mm});
            skArc(sketch, "E79.7", {"start": v(56.15, -48.18) * mm, "mid": v(58.99, -44.68) * mm, "end": v(60, -40.3) * mm});
            skCircle(sketch, "E79.8", {"center": v(60, 67.5) * mm, "radius": 4 * mm});
            skArc(sketch, "E79.9", {"start": v(80, 80) * mm, "mid": v(77.07, 87.07) * mm, "end": v(70, 90) * mm});
            skLineSegment(sketch, "E79.10", {"start": v(-70, 90) * mm, "end": v(70, 90) * mm});
            skArc(sketch, "E79.11", {"start": v(-70, 90) * mm, "mid": v(-77.07, 87.07) * mm, "end": v(-80, 80) * mm});
            skLineSegment(sketch, "E79.12", {"start": v(-80, -80) * mm, "end": v(-80, 80) * mm});
            skCircle(sketch, "E79.13", {"center": v(-60, 67.5) * mm, "radius": 4 * mm});
            skLineSegment(sketch, "E79.14", {"start": v(80, -80) * mm, "end": v(80, 80) * mm});
            skArc(sketch, "E79.15", {"start": v(70, -90) * mm, "mid": v(77.07, -87.07) * mm, "end": v(80, -80) * mm});
            skLineSegment(sketch, "E79.16", {"start": v(-70, -90) * mm, "end": v(70, -90) * mm});
            skArc(sketch, "E79.17", {"start": v(-80, -80) * mm, "mid": v(-77.07, -87.07) * mm, "end": v(-70, -90) * mm});
            skCircle(sketch, "E79.18", {"center": v(-60, -67.5) * mm, "radius": 4 * mm});
            skCircle(sketch, "E79.19", {"center": v(60, -67.5) * mm, "radius": 4 * mm});
            skLineSegment(sketch, "E80", {"start": v(-33, 90) * mm, "end": v(7.9, 90) * mm});
            skCircle(sketch, "E81", {"center": v(0, 120) * mm, "radius": 6 * mm});
            skLineSegment(sketch, "E82", {"start": v(0, 90) * mm, "end": v(0, 120) * mm, "construction": true});
            skArc(sketch, "E83", {"start": v(15, 120) * mm, "mid": v(0, 135) * mm, "end": v(-15, 120) * mm});
            skLineSegment(sketch, "E84", {"start": v(-15, 120) * mm, "end": v(-15, 108) * mm});
            skLineSegment(sketch, "E85", {"start": v(15, 120) * mm, "end": v(15, 108) * mm});
            skLineSegment(sketch, "E86", {"start": v(-15, 108) * mm, "end": v(-33, 90) * mm});
            skLineSegment(sketch, "E87", {"start": v(15, 108) * mm, "end": v(33, 90) * mm});
            skLineSegment(sketch, "E88", {"start": v(-80, 0) * mm, "end": v(80, 0) * mm, "construction": true});
            skLineSegment(sketch, "E89.MirrorCS", {"start": v(15, -108) * mm, "end": v(33, -90) * mm});
            skLineSegment(sketch, "E90.MirrorCS", {"start": v(-15, -108) * mm, "end": v(-33, -90) * mm});
            skLineSegment(sketch, "E91.MirrorCS", {"start": v(0, -90) * mm, "end": v(0, -120) * mm, "construction": true});
            skCircle(sketch, "E92.MirrorC", {"center": v(0, -120) * mm, "radius": 6 * mm});
            skLineSegment(sketch, "E93.MirrorCS", {"start": v(-15, -120) * mm, "end": v(-15, -108) * mm});
            skLineSegment(sketch, "E94.MirrorCS", {"start": v(15, -120) * mm, "end": v(15, -108) * mm});
            skArc(sketch, "E95.MirrorCS", {"start": v(15, -120) * mm, "mid": v(0, -135) * mm, "end": v(-15, -120) * mm});
            skSolve(sketch);
        }
        {
            var Q0;
            Q0 = qSketchRegion(id + "F16", true);
            var Q1;
            Q1=makeQuery(id+"F2.opExtrude","CAP_FACE",FACE,{"disambiguationData":[OSD([sQuery(id+"F0.wireOp",EDGE,"E12"),sQuery(id+"F0.wireOp",EDGE,"E13"),sQuery(id+"F0.wireOp",EDGE,"E14"),sQuery(id+"F0.wireOp",EDGE,"E15"),sQuery(id+"F0.wireOp",EDGE,"E17.filletArc"),sQuery(id+"F0.wireOp",EDGE,"E18.filletArc"),sQuery(id+"F0.wireOp",EDGE,"E19.filletArc"),sQuery(id+"F0.wireOp",EDGE,"E20.filletArc"),sQuery(id+"F0.wireOp",EDGE,"E25.0"),sQuery(id+"F0.wireOp",EDGE,"E25.1"),sQuery(id+"F0.wireOp",EDGE,"E25.2"),sQuery(id+"F0.wireOp",EDGE,"E25.3"),sQuery(id+"F0.wireOp",EDGE,"E25.4"),sQuery(id+"F0.wireOp",EDGE,"E25.5"),sQuery(id+"F0.wireOp",EDGE,"E25.6"),sQuery(id+"F0.wireOp",EDGE,"E25.7")])],"isStart":false});
            extrude(context, id + "F17", {"entities" : qUnion([Q0]), "endBound" : BoundingType.UP_TO_SURFACE, "endBoundEntityFace" : qUnion([Q1]), "depth" : 25 * mm, "offsetDistance" : 25 * mm});
        }
    });
